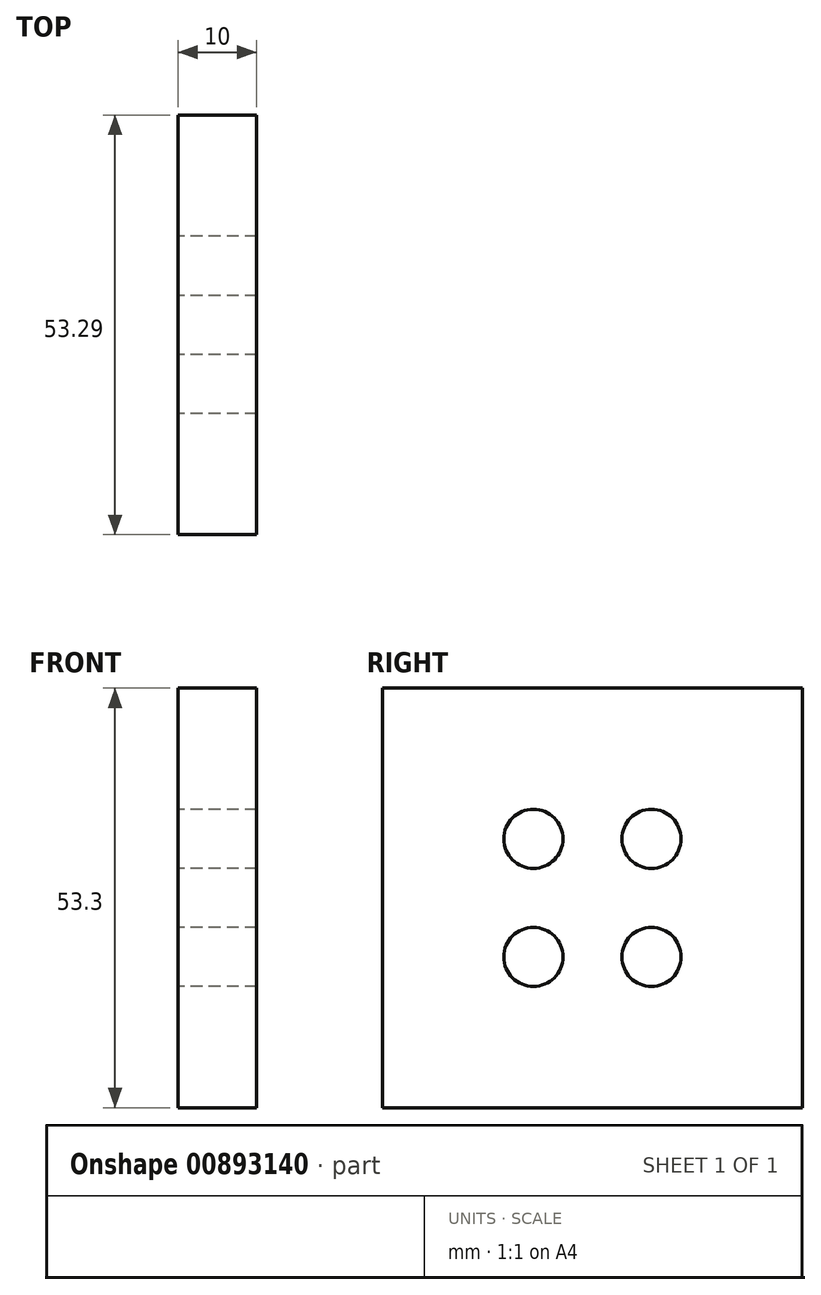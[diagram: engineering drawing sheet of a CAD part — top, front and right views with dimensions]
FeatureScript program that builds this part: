
annotation { "Feature Type Name" : "Feature", "Feature Type Description" : "" }
export const myFeature = defineFeature(function(context is Context, id is Id, definition is map)
    precondition{}
    {
        {
            var Q0;
            Q0=qCreatedBy(makeId("Right.planeOp"),FACE);
            var sketch = newSketch(context, id + "F0", { "sketchPlane" : qUnion([Q0])});
            skPoint(sketch, "E0.endSnap0", {"position": v(3.75, 0) * mm});
            skPoint(sketch, "E0.endSnap1", {"position": v(0, 3.75) * mm});
            skCircle(sketch, "E1", {"center": v(3.75, 3.75) * mm, "radius": 3.75 * mm});
            skPoint(sketch, "E2.endSnap0", {"position": v(3.75, 22.5) * mm});
            skCircle(sketch, "E3", {"center": v(3.75, 18.75) * mm, "radius": 3.75 * mm});
            skCircle(sketch, "E4.MirrorC", {"center": v(18.75, 18.75) * mm, "radius": 3.75 * mm});
            skCircle(sketch, "E5.MirrorC", {"center": v(18.75, 3.75) * mm, "radius": 3.75 * mm});
            skLineSegment(sketch, "E6.0", {"start": v(-4.15, 26.65) * mm, "end": v(-4.15, -4.15) * mm});
            skLineSegment(sketch, "E7.0", {"start": v(26.65, 26.65) * mm, "end": v(26.65, -4.15) * mm});
            skLineSegment(sketch, "E8.0", {"start": v(11.25, -4.15) * mm, "end": v(26.65, -4.15) * mm});
            skLineSegment(sketch, "E9.0", {"start": v(26.65, -4.15) * mm, "end": v(-4.15, -4.15) * mm});
            skLineSegment(sketch, "E10.0", {"start": v(11.25, 26.65) * mm, "end": v(26.65, 26.65) * mm});
            skLineSegment(sketch, "E11.0", {"start": v(26.65, 26.65) * mm, "end": v(-4.15, 26.65) * mm});
            skPoint(sketch, "E12.orphan", {"position": v(26.65, 45) * mm});
            skPoint(sketch, "E13.orphan", {"position": v(-4.15, 45) * mm});
            skPoint(sketch, "E14.orphan", {"position": v(-4.15, 11.25) * mm});
            skLineSegment(sketch, "E15.0", {"start": v(37.9, 26.65) * mm, "end": v(37.9, -4.15) * mm});
            skLineSegment(sketch, "E16", {"start": v(-4.15, -4.15) * mm, "end": v(-15.4, -4.15) * mm});
            skLineSegment(sketch, "E17", {"start": v(-15.4, -4.15) * mm, "end": v(-15.4, 26.65) * mm});
            skLineSegment(sketch, "E18", {"start": v(-15.4, 26.65) * mm, "end": v(37.9, 26.65) * mm});
            skLineSegment(sketch, "E19", {"start": v(37.9, -4.15) * mm, "end": v(26.65, -4.15) * mm});
            skLineSegment(sketch, "E20.0", {"start": v(26.65, -15.4) * mm, "end": v(-4.15, -15.4) * mm});
            skLineSegment(sketch, "E21.0", {"start": v(37.9, -15.4) * mm, "end": v(26.65, -15.4) * mm});
            skLineSegment(sketch, "E22.0", {"start": v(-4.15, -15.4) * mm, "end": v(-15.4, -15.4) * mm});
            skLineSegment(sketch, "E23.0", {"start": v(-15.4, 37.9) * mm, "end": v(37.9, 37.9) * mm});
            skLineSegment(sketch, "E24", {"start": v(37.9, 37.9) * mm, "end": v(37.9, 26.65) * mm});
            skLineSegment(sketch, "E25", {"start": v(37.9, -4.15) * mm, "end": v(37.9, -15.4) * mm});
            skLineSegment(sketch, "E26", {"start": v(-15.4, -15.4) * mm, "end": v(-15.4, -4.15) * mm});
            skLineSegment(sketch, "E27", {"start": v(-15.4, 26.65) * mm, "end": v(-15.4, 37.9) * mm});
            skSolve(sketch);
        }
        {
            var Q0;
            Q0=makeQuery(id+"F0.imprint","IMPRINT",FACE,{"disambiguationData":[TD([[makeQuery(id+"F0.imprint","IMPRINT",EDGE,{"derivedFrom":sQuery(id+"F0.wireOp",EDGE,"E1")}),-1.0]])]});
            var Q1;
            {var subQ0=sQuery(id+"F0.wireOp",EDGE,"E7.0");Q1=makeQuery(id+"F0.imprint","IMPRINT",FACE,{"disambiguationData":[TD([[makeQuery(id+"F0.imprint","IMPRINT",EDGE,{"derivedFrom":subQ0}),1.0]])]});}
            var Q2;
            {var subQ1=sQuery(id+"F0.wireOp",EDGE,"E16");Q2=makeQuery(id+"F0.imprint","IMPRINT",FACE,{"disambiguationData":[TD([[makeQuery(id+"F0.imprint","IMPRINT",EDGE,{"derivedFrom":subQ1}),1.0]])]});}
            var Q3;
            Q3=makeQuery(id+"F0.imprint","IMPRINT",FACE,{"disambiguationData":[TD([[makeQuery(id+"F0.imprint","IMPRINT",EDGE,{"derivedFrom":sQuery(id+"F0.wireOp",EDGE,"E23.0")}),-1.0]])]});
            var Q4;
            {var subQ0=sQuery(id+"F0.wireOp",EDGE,"E6.0");Q4=makeQuery(id+"F0.imprint","IMPRINT",FACE,{"disambiguationData":[TD([[makeQuery(id+"F0.imprint","IMPRINT",EDGE,{"derivedFrom":subQ0}),-1.0]])]});}
            extrude(context, id + "F1", {"entities" : qUnion([Q0, Q1, Q2, Q3, Q4]), "depth" : 10 * mm, "offsetDistance" : 25 * mm});
        }
    });
